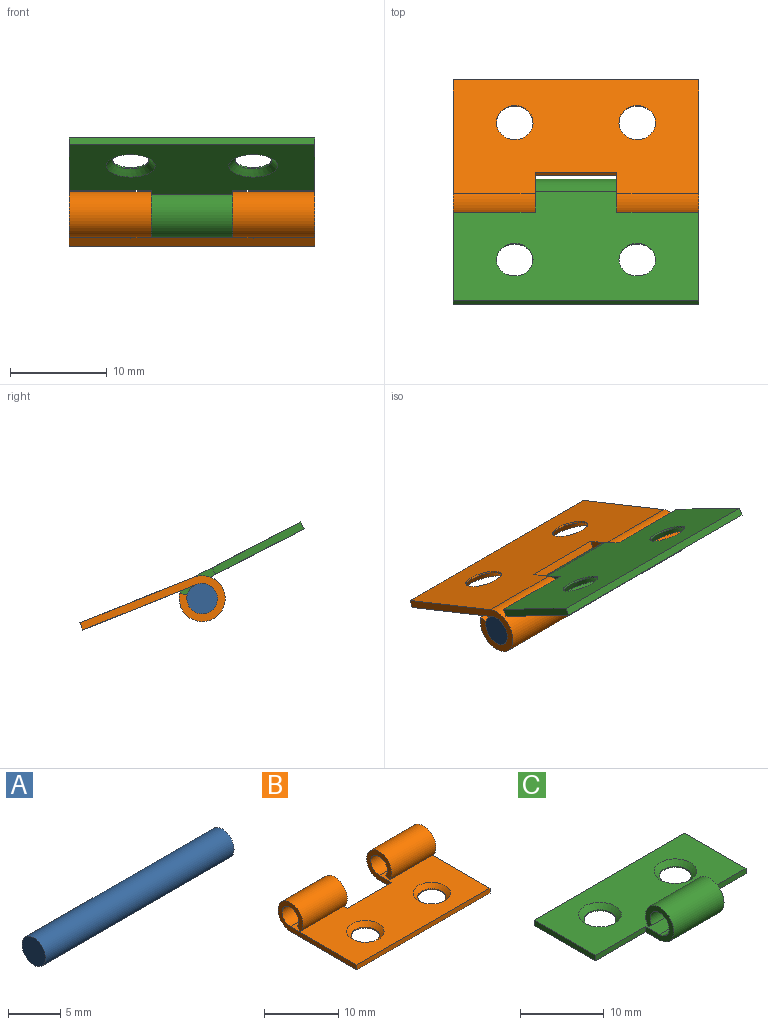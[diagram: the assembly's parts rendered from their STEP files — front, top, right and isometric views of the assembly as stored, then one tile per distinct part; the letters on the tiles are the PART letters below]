
ASSEMBLY  parts=3 mates=2
PART A: 3 faces, bbox 25.4x3.2x3.2 mm
  f0: plane 3.18x3.18mm, normal (1,0,0), area 7.9mm2, adj f1
  f1: cylinder r=1.59mm len=25.4mm, axis (-1,0,0), area 253.4mm2, adj f0,f2
  f2: plane 3.18x3.18mm, normal (-1,0,0), area 7.9mm2, adj f1
PART B: 18 faces, bbox 25.4x15.1x4.8 mm
  f0: plane 8.47x0.65mm, normal (0,0.57,-0.82), area 6.7mm2, adj f3,f6,f8,f15
  f1: plane 8.47x0.65mm, normal (0,0.57,-0.82), area 6.7mm2, adj f4,f7,f10,f17
  f2: plane 25.4x12.7mm, normal (0,0,1), area 262.1mm2, adj f3,f4,f8,f9,f10,f13,f14,f15
  f3: cylinder r=1.59mm len=8.47mm, axis (1,0,0), area 71.5mm2, adj f0,f2,f8,f15
  f4: cylinder r=1.59mm len=8.47mm, axis (1,0,0), area 71.5mm2, adj f1,f2,f10,f17
  f5: plane 25.4x12.7mm, normal (0,0,-1), area 279.8mm2, adj f6,f7,f8,f9,f10,f11,f12,f15
  f6: cylinder r=2.38mm len=8.47mm, axis (1,0,0), area 107.3mm2, adj f0,f5,f8,f15
  f7: cylinder r=2.38mm len=8.47mm, axis (1,0,0), area 107.3mm2, adj f1,f5,f10,f17
  f8: plane 15.08x4.76mm, normal (-1,0,0), area 18.5mm2, adj f0,f2,f3,f5,f6,f9
  f9: plane 25.4x0.79mm, normal (0,-1,0), area 20.2mm2, adj f2,f5,f8,f10
  f10: plane 15.08x4.76mm, normal (1,0,0), area 18.5mm2, adj f1,f2,f4,f5,f7,f9
  f11: cylinder r=1.9mm len=3.8mm, axis (0,0,1), area 1.9mm2, adj f5,f14
  f12: cylinder r=1.9mm len=3.8mm, axis (0,0,1), area 1.9mm2, adj f5,f13
  f13: cone r=1.9mm half-angle=45deg, axis (0,0,1), area 12.5mm2, adj f2,f12
  f14: cone r=1.9mm half-angle=45deg, axis (0,0,1), area 12.5mm2, adj f2,f11
  f15: plane 4.76x4.76mm, normal (1,0,0), area 10.3mm2, adj f0,f2,f3,f5,f6,f16
  f16: plane 8.47x0.79mm, normal (0,1,0), area 6.7mm2, adj f2,f5,f15,f17
  f17: plane 4.76x4.76mm, normal (-1,0,0), area 10.3mm2, adj f1,f2,f4,f5,f7,f16
PART C: 16 faces, bbox 25.4x15.1x4.8 mm
  f0: plane 10.32x0.79mm, normal (-1,0,0), area 8.2mm2, adj f1,f2,f4,f15
  f1: plane 25.4x12.7mm, normal (0,0,1), area 241.9mm2, adj f0,f4,f5,f6,f10,f11,f12,f13
  f2: plane 25.4x12.7mm, normal (0,0,-1), area 259.6mm2, adj f0,f4,f5,f7,f8,f9,f12,f13
  f3: plane 8.47x0.65mm, normal (0,-0.57,-0.82), area 6.7mm2, adj f6,f7,f13,f14
  f4: plane 25.4x0.79mm, normal (0,1,0), area 20.2mm2, adj f0,f1,f2,f5
  f5: plane 10.32x0.79mm, normal (1,0,0), area 8.2mm2, adj f1,f2,f4,f12
  f6: cylinder r=1.59mm len=8.47mm, axis (1,0,0), area 71.5mm2, adj f1,f3,f13,f14
  f7: cylinder r=2.38mm len=8.47mm, axis (1,0,0), area 107.3mm2, adj f2,f3,f13,f14
  f8: cylinder r=1.9mm len=3.8mm, axis (0,0,1), area 1.9mm2, adj f2,f11
  f9: cylinder r=1.9mm len=3.8mm, axis (0,0,1), area 1.9mm2, adj f2,f10
  f10: cone r=1.9mm half-angle=45deg, axis (0,0,1), area 12.5mm2, adj f1,f9
  f11: cone r=1.9mm half-angle=45deg, axis (0,0,1), area 12.5mm2, adj f1,f8
  f12: plane 8.47x0.79mm, normal (0,-1,0), area 6.7mm2, adj f1,f2,f5,f13
  f13: plane 4.76x4.76mm, normal (1,0,0), area 10.3mm2, adj f1,f2,f3,f6,f7,f12
  f14: plane 4.76x4.76mm, normal (-1,0,0), area 10.3mm2, adj f1,f2,f3,f6,f7,f15
  f15: plane 8.47x0.79mm, normal (0,-1,0), area 6.7mm2, adj f0,f1,f2,f14
PLACE A t=(-7.62,-12.32,-2.37)mm fixed
PLACE B rot(axis=(1,0,0),158.1deg) t=(-7.62,-12.32,-2.37)mm
PLACE C rot(axis=(1,0,0),152.7deg) t=(-7.62,-12.32,-2.37)mm
MATE revolute B.f3 <-> A.f1  axis (1,0,0) through (5.08,-12.32,-2.37)mm
MATE revolute C.f6 <-> A.f1  axis (1,0,0) through (-7.62,-12.32,-2.37)mm
